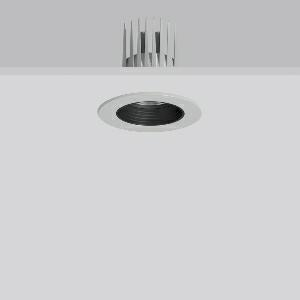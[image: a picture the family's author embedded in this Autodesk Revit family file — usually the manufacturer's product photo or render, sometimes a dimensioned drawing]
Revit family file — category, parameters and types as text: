
# Revit family: heledon_mini_e_901743_004_76_7bc1
name_source: partatom
category: Lighting Fixtures
units: mm (PartAtom-declared; Revit-internal decimal feet)

## family parameters
Cut with Voids When Loaded = No
Host = Face
Light Source = No
Part Type = Normal
Room Calculation Point = No
Round Connector Dimension = Use Diameter
Shared = No

## types (1)
- HELEDON mini E (1 x LED Modul 930, 2250 lm, 3000)
    Apparent Load = 20 VA
    Approval mark = CE
    CIE Flux Codes = 99 100 100 100 100
    Color Rendering = 90
    Color Temperature = 3000
    Default Elevation = 1800 mm
    Description = Series: HELEDON mini
Round recessed downlight. Housing: die-cast aluminium, powder-coated. Black plastic ring and recessed LED to prevent glare from the side. Optical assembly with lens made of plastic (polycarbonate) for the best homogeneous light distribution - can be changed without tools. Best colour rendering index Ra>90. Suitable for Recessed ceiling mounting. Installation without tools thanks to spring fastening system. Including separate LED converter with connecting cable 600 mm.High quality converter without flickering and stroboscopic effect. Through-wiring box (5 pole) available as accessory. The following accessories can be mounted without use of tools: interchangeable lenses, decorative glasses, honeycomb louvre, clear and frosted diffusers, white interchangeable plastic ring. 
Colour: silver
Diameter: 124 mm
Height: 3 mm
Cut-out diameter: 114 mm
Recess height: 170 mm
Luminaire: recess height: 120 mm
Lamp: LED
Socket: without socket
Colour temperature: 3000K
Colour rendering index (CRI): 92
System power: 20 W
Rated luminous flux: 2250 lm
Luminous efficiency: 113 lm/W
Control gear: Converter, dimmable, DALI
Protection class: II
Type of protection: IP 20
    Height = 0 mm  [stored 0 ft]
    Lamp = 1 x LED Modul 930
    Lamp Light Flux = 2250 lm
    Lamp count = 1
    Length = 124 mm  [stored 0.406824 ft]
    Lifetime = 50000 h
    Luminous efficacy = 113 lm/W
    Manufacturer = RZB
    ModVariant = No
    Model = 901743.004.76
    Mounting Place = Ceiling
    Mounting Type = Recessed
    Number of Poles = 1
    OnlyDefault = Yes
    Power Factor = 1
    Product Name = HELEDON mini E
    Product group = Recessed downlights
    ProductGroupID = 402
    Protection Class = Protection class II
    Protection Degree = IP 20
    RLX_Detail_Level = 1
    RLX_Emergency_Light_Flux = 0 lm
    RLX_Emergency_Type = 0
    RLX_Emergency_Type_DB = No
    RlxData = <blob elided: 126881 chars, md5=ed876f8f>
    Socket = socket
    Standby Power = 0 W
    System Light Flux = 2250 lm
    System Power = 20 W
    Type Comments = Product without accessories
    Type Image = 901656.004.jpg
    URL = http://relux.com
    VarID = ---
    Voltage = 230 V
    Voltage Range = 220-240 V
    Weight = 0.00 kg
    Width = 0 mm  [stored 0 ft]

note: [stored X ft] marks values corroborated as IEEE doubles in the binary element streams (Revit-internal decimal feet)

## geometry (parser evidence)
native form markers: Blend x4, Sweep x12
no freeform markers — native parametric forms only
